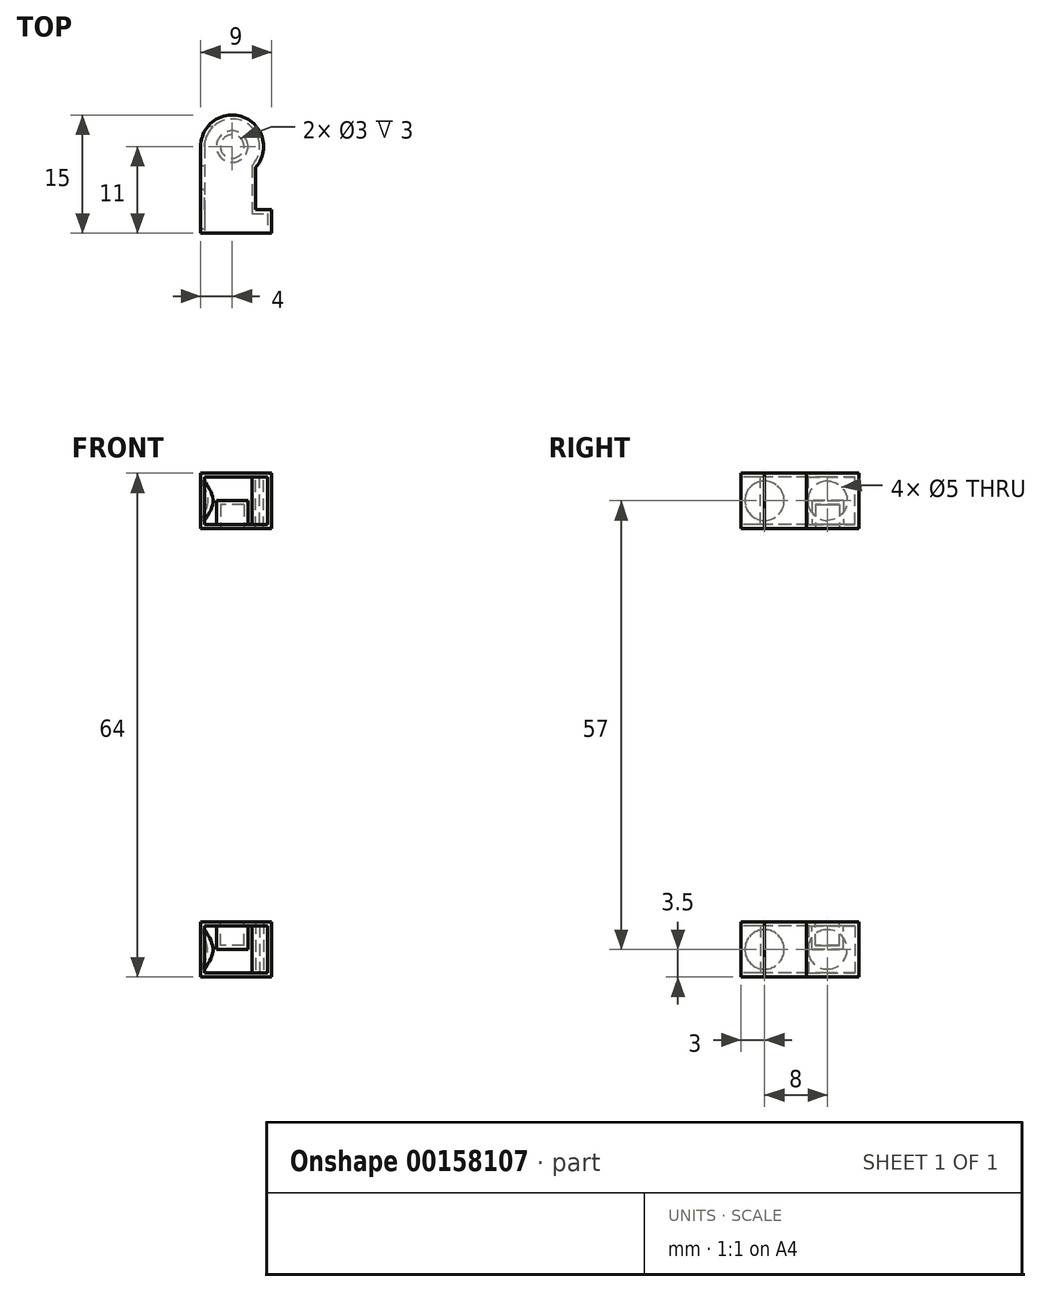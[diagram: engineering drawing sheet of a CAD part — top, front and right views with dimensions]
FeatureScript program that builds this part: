
annotation { "Feature Type Name" : "Feature", "Feature Type Description" : "" }
export const myFeature = defineFeature(function(context is Context, id is Id, definition is map)
    precondition{}
    {
        {
            var Q0;
            Q0=qCreatedBy(makeId("Top.planeOp"),FACE);
            var sketch = newSketch(context, id + "F0", { "sketchPlane" : qUnion([Q0])});
            skLineSegment(sketch, "E0.left", {"start": v(-4, 8) * mm, "end": v(-4, -3) * mm});
            skLineSegment(sketch, "E0.right", {"start": v(3, 5.35) * mm, "end": v(3, 0) * mm});
            skLineSegment(sketch, "E1.bottom", {"start": v(3, 0) * mm, "end": v(5, 0) * mm});
            skLineSegment(sketch, "E2", {"start": v(5, 0) * mm, "end": v(5, -3) * mm});
            skLineSegment(sketch, "E3", {"start": v(5, -3) * mm, "end": v(-4, -3) * mm});
            skCircle(sketch, "E4", {"center": v(0, 8) * mm, "radius": 4 * mm});
            skSolve(sketch);
        }
        {
            var Q0;
            {var subQ1=sQuery(id+"F0.wireOp",EDGE,"E0.left");Q0=makeQuery(id+"F0.imprint","IMPRINT",FACE,{"disambiguationData":[TD([[makeQuery(id+"F0.imprint","IMPRINT",EDGE,{"derivedFrom":subQ1}),1.0]])]});}
            var Q1;
            {var subQ0=sQuery(id+"F0.wireOp",EDGE,"E4");var subQ1=makeQuery(id+"F0.imprint","INTERSECT",VERTEX,{"derivedFrom":[sQuery(id+"F0.wireOp",EDGE,"E0.left"),subQ0]});Q1=makeQuery(id+"F0.imprint","IMPRINT",FACE,{"disambiguationData":[TD([[makeQuery(id+"F0.imprint","IMPRINT",EDGE,{"disambiguationData":[TD([[subQ1,-1.0]])],"derivedFrom":subQ0}),1.0]])]});}
            extrude(context, id + "F1", {"entities" : qUnion([Q0, Q1]), "depth" : 7 * mm});
        }
        {
            var Q0;
            Q0=makeQuery(id+"F1.opExtrude","CAP_FACE",FACE,{"disambiguationData":[OSD([sQuery(id+"F0.wireOp",EDGE,"E0.left"),sQuery(id+"F0.wireOp",EDGE,"E0.right"),sQuery(id+"F0.wireOp",EDGE,"E1.bottom"),sQuery(id+"F0.wireOp",EDGE,"E2"),sQuery(id+"F0.wireOp",EDGE,"E3"),sQuery(id+"F0.wireOp",EDGE,"E4")])],"isStart":false});
            var sketch = newSketch(context, id + "F2", { "sketchPlane" : qUnion([Q0])});
            skCircle(sketch, "E5", {"center": v(0, 8) * mm, "radius": 1.5 * mm});
            skSolve(sketch);
        }
        {
            var Q0;
            Q0=makeQuery(id+"F2.imprint","IMPRINT",FACE,{"disambiguationData":[TD([[makeQuery(id+"F2.imprint","IMPRINT",EDGE,{"derivedFrom":sQuery(id+"F2.wireOp",EDGE,"E5")}),1.0]])]});
            extrude(context, id + "F3", {"entities" : qUnion([Q0]), "operationType" : NewBodyOperationType.REMOVE, "oppositeDirection" : true, "depth" : 3 * mm});
        }
        {
            var Q0;
            Q0=makeQuery(id+"F1.opExtrude","SWEPT_FACE",FACE,{"disambiguationData":[OSD([sQuery(id+"F0.wireOp",EDGE,"E3")])]});
            shell(context, id + "F4", {"entities" : qUnion([Q0]), "thickness" : 0.5 * mm});
        }
        {
            var Q0;
            Q0=makeQuery(id+"F1.opExtrude","SWEPT_FACE",FACE,{"disambiguationData":[OSD([sQuery(id+"F0.wireOp",EDGE,"E0.left")])]});
            var sketch = newSketch(context, id + "F5", { "sketchPlane" : qUnion([Q0])});
            skCircle(sketch, "E6", {"center": v(0, 3.5) * mm, "radius": 2.5 * mm});
            skCircle(sketch, "E7", {"center": v(-8, 3.5) * mm, "radius": 2.5 * mm});
            skLineSegment(sketch, "E8", {"start": v(-8, 3.5) * mm, "end": v(3, 3.5) * mm, "construction": true});
            skSolve(sketch);
        }
        {
            var Q0;
            {var subQ0=sQuery(id+"F5.wireOp",EDGE,"E7");var subQ1=makeQuery(id+"F1.opExtrude","SWEPT_EDGE",EDGE,{"disambiguationData":[OSD([sQuery(id+"F0.wireOp",EDGE,"E0.left"),sQuery(id+"F0.wireOp",EDGE,"E4")])]});var subQ2=makeQuery(id+"F5.imprint","INTERSECT",VERTEX,{"disambiguationData":[OD(0.0)],"derivedFrom":[subQ1,subQ0]});Q0=makeQuery(id+"F5.imprint","IMPRINT",FACE,{"disambiguationData":[TD([[makeQuery(id+"F5.imprint","IMPRINT",EDGE,{"disambiguationData":[TD([[subQ2,1.0]])],"derivedFrom":subQ0}),1.0]])]});}
            var Q1;
            Q1=makeQuery(id+"F5.imprint","IMPRINT",FACE,{"disambiguationData":[TD([[makeQuery(id+"F5.imprint","IMPRINT",EDGE,{"derivedFrom":sQuery(id+"F5.wireOp",EDGE,"E6")}),1.0]])]});
            var Q2;
            {var subQ0=sQuery(id+"F5.wireOp",EDGE,"E7");var subQ1=makeQuery(id+"F1.opExtrude","SWEPT_EDGE",EDGE,{"disambiguationData":[OSD([sQuery(id+"F0.wireOp",EDGE,"E0.left"),sQuery(id+"F0.wireOp",EDGE,"E4")])]});var subQ2=makeQuery(id+"F5.imprint","INTERSECT",VERTEX,{"disambiguationData":[OD(0.0)],"derivedFrom":[subQ1,subQ0]});Q2=makeQuery(id+"F5.imprint","IMPRINT",FACE,{"disambiguationData":[TD([[makeQuery(id+"F5.imprint","IMPRINT",EDGE,{"disambiguationData":[TD([[subQ2,-1.0]])],"derivedFrom":subQ0}),1.0]])]});}
            extrude(context, id + "F6", {"entities" : qUnion([Q0, Q1, Q2]), "operationType" : NewBodyOperationType.REMOVE, "oppositeDirection" : true, "depth" : 2 * mm});
        }
        {
            var Q0;
            Q0=makeQuery(id+"F1.opExtrude","CAP_FACE",FACE,{"disambiguationData":[OSD([sQuery(id+"F0.wireOp",EDGE,"E0.left"),sQuery(id+"F0.wireOp",EDGE,"E0.right"),sQuery(id+"F0.wireOp",EDGE,"E1.bottom"),sQuery(id+"F0.wireOp",EDGE,"E2"),sQuery(id+"F0.wireOp",EDGE,"E3"),sQuery(id+"F0.wireOp",EDGE,"E4")])],"isStart":false});
            cPlane(context, id + "F7", {"entities" : qUnion([Q0]), "cplaneType" : CPlaneType.OFFSET, "offset" : 25 * mm, "width" : 150 * mm, "height" : 150 * mm});
        }
        {
            var Q0;
            Q0=makeQuery(id+"F1.opExtrude","SWEPT_BODY",BODY,{"disambiguationData":[OSD([sQuery(id+"F0.wireOp",EDGE,"E0.left"),sQuery(id+"F0.wireOp",EDGE,"E0.right"),sQuery(id+"F0.wireOp",EDGE,"E1.bottom"),sQuery(id+"F0.wireOp",EDGE,"E2"),sQuery(id+"F0.wireOp",EDGE,"E3"),sQuery(id+"F0.wireOp",EDGE,"E4")])]});
            var Q1;
            Q1=qCreatedBy(id+"F7.planeOp",FACE);
            mirror(context, id + "F8", {"entities" : qUnion([Q0]), "mirrorPlane" : qUnion([Q1])});
        }
    });
